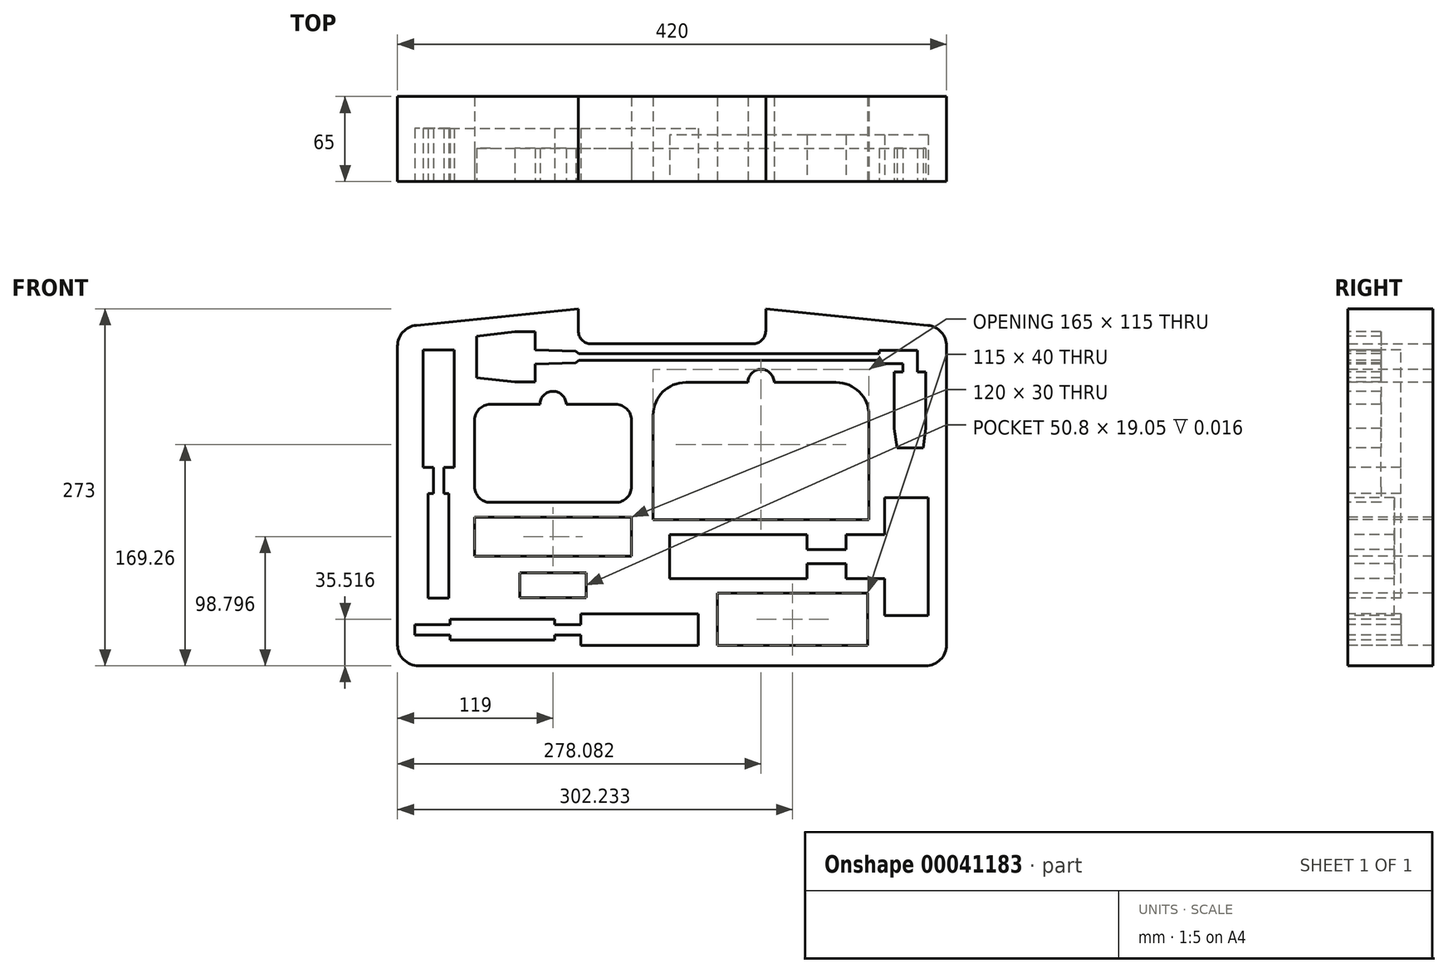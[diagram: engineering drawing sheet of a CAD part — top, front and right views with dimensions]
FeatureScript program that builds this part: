
annotation { "Feature Type Name" : "Feature", "Feature Type Description" : "" }
export const myFeature = defineFeature(function(context is Context, id is Id, definition is map)
    precondition{}
    {
        {
            var Q0;
            Q0=qCreatedBy(makeId("Front.planeOp"),FACE);
            var sketch = newSketch(context, id + "F0", { "sketchPlane" : qUnion([Q0])});
            skLineSegment(sketch, "E0.rect.top", {"start": v(0, -129.5) * mm, "end": v(-194, -129.5) * mm});
            skPoint(sketch, "E0.rect.middle", {"position": v(0, 0) * mm});
            skLineSegment(sketch, "E1", {"start": v(0, -129.5) * mm, "end": v(0, 143.5) * mm, "construction": true});
            skLineSegment(sketch, "E2", {"start": v(0, 143.5) * mm, "end": v(-71.7, 143.5) * mm, "construction": true});
            skLineSegment(sketch, "E3", {"start": v(-71.7, 143.5) * mm, "end": v(-71.7, 126.7) * mm});
            skLineSegment(sketch, "E4", {"start": v(-61.7, 116.7) * mm, "end": v(0, 116.7) * mm});
            skLineSegment(sketch, "E5", {"start": v(-71.7, 143.5) * mm, "end": v(-195.61, 130.96) * mm});
            skLineSegment(sketch, "E6", {"start": v(-210, -113.5) * mm, "end": v(-210, 115.04) * mm});
            skPoint(sketch, "E7", {"position": v(-210, 0) * mm});
            skPoint(sketch, "E8.visualSharp", {"position": v(-210, -129.5) * mm});
            skArc(sketch, "E8.filletArc", {"start": v(-210, -113.5) * mm, "mid": v(-205.31, -124.81) * mm, "end": v(-194, -129.5) * mm});
            skPoint(sketch, "E9.visualSharp", {"position": v(-210, 129.5) * mm});
            skArc(sketch, "E9.filletArc", {"start": v(-195.61, 130.96) * mm, "mid": v(-205.87, 125.77) * mm, "end": v(-210, 115.04) * mm});
            skPoint(sketch, "E10.visualSharp", {"position": v(-71.7, 116.7) * mm});
            skArc(sketch, "E10.filletArc", {"start": v(-71.7, 126.7) * mm, "mid": v(-68.77, 119.63) * mm, "end": v(-61.7, 116.7) * mm});
            skLineSegment(sketch, "E11.MirrorCS", {"start": v(71.7, 143.5) * mm, "end": v(71.7, 126.7) * mm});
            skArc(sketch, "E12.MirrorCS", {"start": v(71.7, 126.7) * mm, "mid": v(68.77, 119.63) * mm, "end": v(61.7, 116.7) * mm});
            skArc(sketch, "E13.MirrorCS", {"start": v(195.61, 130.96) * mm, "mid": v(205.87, 125.77) * mm, "end": v(210, 115.04) * mm});
            skArc(sketch, "E14.MirrorCS", {"start": v(210, -113.5) * mm, "mid": v(205.31, -124.81) * mm, "end": v(194, -129.5) * mm});
            skLineSegment(sketch, "E15.MirrorCS", {"start": v(0, -129.5) * mm, "end": v(194, -129.5) * mm});
            skPoint(sketch, "E16.MirrorP", {"position": v(210, -129.5) * mm});
            skPoint(sketch, "E17.MirrorP", {"position": v(210, 0) * mm});
            skLineSegment(sketch, "E18.MirrorCS", {"start": v(0, 143.5) * mm, "end": v(71.7, 143.5) * mm});
            skPoint(sketch, "E19.MirrorP", {"position": v(210, 129.5) * mm});
            skLineSegment(sketch, "E20.MirrorCS", {"start": v(210, -113.5) * mm, "end": v(210, 115.04) * mm});
            skLineSegment(sketch, "E21.MirrorCS", {"start": v(61.7, 116.7) * mm, "end": v(0, 116.7) * mm});
            skPoint(sketch, "E22.MirrorP", {"position": v(71.7, 116.7) * mm});
            skLineSegment(sketch, "E23.MirrorCS", {"start": v(71.7, 143.5) * mm, "end": v(195.61, 130.96) * mm});
            skSolve(sketch);
        }
        {
            var Q0;
            Q0=makeQuery(id+"F0.imprint","IMPRINT",FACE,{"disambiguationData":[TD([[makeQuery(id+"F0.imprint","IMPRINT",EDGE,{"derivedFrom":sQuery(id+"F0.wireOp",EDGE,"E0.rect.top")}),-1.0]])]});
            extrude(context, id + "F1", {"entities" : qUnion([Q0]), "depth" : 65 * mm});
        }
        {
            var Q0;
            Q0=makeQuery(id+"F1.opExtrude","CAP_FACE",FACE,{"disambiguationData":[OSD([sQuery(id+"F0.wireOp",EDGE,"E0.rect.top"),sQuery(id+"F0.wireOp",EDGE,"E3"),sQuery(id+"F0.wireOp",EDGE,"E4"),sQuery(id+"F0.wireOp",EDGE,"E5"),sQuery(id+"F0.wireOp",EDGE,"E6"),sQuery(id+"F0.wireOp",EDGE,"E8.filletArc"),sQuery(id+"F0.wireOp",EDGE,"E9.filletArc"),sQuery(id+"F0.wireOp",EDGE,"E10.filletArc"),sQuery(id+"F0.wireOp",EDGE,"E11.MirrorCS"),sQuery(id+"F0.wireOp",EDGE,"E12.MirrorCS"),sQuery(id+"F0.wireOp",EDGE,"E13.MirrorCS"),sQuery(id+"F0.wireOp",EDGE,"E14.MirrorCS"),sQuery(id+"F0.wireOp",EDGE,"E15.MirrorCS"),sQuery(id+"F0.wireOp",EDGE,"E20.MirrorCS"),sQuery(id+"F0.wireOp",EDGE,"E21.MirrorCS"),sQuery(id+"F0.wireOp",EDGE,"E23.MirrorCS")])],"isStart":false});
            var sketch = newSketch(context, id + "F2", { "sketchPlane" : qUnion([Q0])});
            skLineSegment(sketch, "E24.bottom", {"start": v(-14.42, -17.74) * mm, "end": v(55.03, -17.74) * mm});
            skLineSegment(sketch, "E24.top", {"start": v(10.58, 87.26) * mm, "end": v(58.08, 87.26) * mm});
            skLineSegment(sketch, "E24.left", {"start": v(-14.42, -17.74) * mm, "end": v(-14.42, 62.26) * mm});
            skLineSegment(sketch, "E24.right", {"start": v(150.58, -17.74) * mm, "end": v(150.58, 62.26) * mm});
            skPoint(sketch, "E25.visualSharp", {"position": v(-14.42, 87.26) * mm});
            skArc(sketch, "E25.filletArc", {"start": v(10.58, 87.26) * mm, "mid": v(-7.1, 79.94) * mm, "end": v(-14.42, 62.26) * mm});
            skPoint(sketch, "E26.visualSharp", {"position": v(150.58, 87.26) * mm});
            skArc(sketch, "E26.filletArc", {"start": v(150.58, 62.26) * mm, "mid": v(143.26, 79.94) * mm, "end": v(125.58, 87.26) * mm});
            skArc(sketch, "E27", {"start": v(78.08, 87.26) * mm, "mid": v(68.08, 97.26) * mm, "end": v(58.08, 87.26) * mm});
            skLineSegment(sketch, "E28.trimOffspring", {"start": v(78.08, 87.26) * mm, "end": v(125.58, 87.26) * mm});
            skLineSegment(sketch, "E29.trimOffspring", {"start": v(55.03, -17.74) * mm, "end": v(150.58, -17.74) * mm});
            skSolve(sketch);
        }
        {
            var Q0;
            Q0=makeQuery(id+"F1.opExtrude","CAP_FACE",FACE,{"disambiguationData":[OSD([sQuery(id+"F0.wireOp",EDGE,"E0.rect.top"),sQuery(id+"F0.wireOp",EDGE,"E3"),sQuery(id+"F0.wireOp",EDGE,"E4"),sQuery(id+"F0.wireOp",EDGE,"E5"),sQuery(id+"F0.wireOp",EDGE,"E6"),sQuery(id+"F0.wireOp",EDGE,"E8.filletArc"),sQuery(id+"F0.wireOp",EDGE,"E9.filletArc"),sQuery(id+"F0.wireOp",EDGE,"E10.filletArc"),sQuery(id+"F0.wireOp",EDGE,"E11.MirrorCS"),sQuery(id+"F0.wireOp",EDGE,"E12.MirrorCS"),sQuery(id+"F0.wireOp",EDGE,"E13.MirrorCS"),sQuery(id+"F0.wireOp",EDGE,"E14.MirrorCS"),sQuery(id+"F0.wireOp",EDGE,"E15.MirrorCS"),sQuery(id+"F0.wireOp",EDGE,"E20.MirrorCS"),sQuery(id+"F0.wireOp",EDGE,"E21.MirrorCS"),sQuery(id+"F0.wireOp",EDGE,"E23.MirrorCS")])],"isStart":false});
            var sketch = newSketch(context, id + "F3", { "sketchPlane" : qUnion([Q0])});
            skLineSegment(sketch, "E30.bottom", {"start": v(-139, -4.53) * mm, "end": v(-101.01, -4.53) * mm});
            skLineSegment(sketch, "E30.top", {"start": v(-139, 70.47) * mm, "end": v(-101, 70.47) * mm});
            skLineSegment(sketch, "E30.left", {"start": v(-151, 7.47) * mm, "end": v(-151, 58.47) * mm});
            skLineSegment(sketch, "E30.right", {"start": v(-31, 7.47) * mm, "end": v(-31, 58.47) * mm});
            skPoint(sketch, "E31.visualSharp", {"position": v(-151, 70.47) * mm});
            skArc(sketch, "E31.filletArc", {"start": v(-139, 70.47) * mm, "mid": v(-147.49, 66.96) * mm, "end": v(-151, 58.47) * mm});
            skPoint(sketch, "E32.visualSharp", {"position": v(-151, -4.53) * mm});
            skArc(sketch, "E32.filletArc", {"start": v(-151, 7.47) * mm, "mid": v(-147.49, -1.01) * mm, "end": v(-139, -4.53) * mm});
            skPoint(sketch, "E33.visualSharp", {"position": v(-31, 70.47) * mm});
            skArc(sketch, "E33.filletArc", {"start": v(-31, 58.47) * mm, "mid": v(-34.51, 66.96) * mm, "end": v(-43, 70.47) * mm});
            skPoint(sketch, "E34.visualSharp", {"position": v(-31, -4.53) * mm});
            skArc(sketch, "E34.filletArc", {"start": v(-43, -4.53) * mm, "mid": v(-34.51, -1.01) * mm, "end": v(-31, 7.47) * mm});
            skArc(sketch, "E35", {"start": v(-81, 70.47) * mm, "mid": v(-91, 80.47) * mm, "end": v(-101, 70.47) * mm});
            skLineSegment(sketch, "E36.trimOffspring", {"start": v(-81, 70.47) * mm, "end": v(-43, 70.47) * mm});
            skLineSegment(sketch, "E37.trimOffspring", {"start": v(-101.01, -4.53) * mm, "end": v(-43, -4.53) * mm});
            skSolve(sketch);
        }
        {
            var Q0;
            Q0=makeQuery(id+"F1.opExtrude","CAP_FACE",FACE,{"disambiguationData":[OSD([sQuery(id+"F0.wireOp",EDGE,"E0.rect.top"),sQuery(id+"F0.wireOp",EDGE,"E3"),sQuery(id+"F0.wireOp",EDGE,"E4"),sQuery(id+"F0.wireOp",EDGE,"E5"),sQuery(id+"F0.wireOp",EDGE,"E6"),sQuery(id+"F0.wireOp",EDGE,"E8.filletArc"),sQuery(id+"F0.wireOp",EDGE,"E9.filletArc"),sQuery(id+"F0.wireOp",EDGE,"E10.filletArc"),sQuery(id+"F0.wireOp",EDGE,"E11.MirrorCS"),sQuery(id+"F0.wireOp",EDGE,"E12.MirrorCS"),sQuery(id+"F0.wireOp",EDGE,"E13.MirrorCS"),sQuery(id+"F0.wireOp",EDGE,"E14.MirrorCS"),sQuery(id+"F0.wireOp",EDGE,"E15.MirrorCS"),sQuery(id+"F0.wireOp",EDGE,"E20.MirrorCS"),sQuery(id+"F0.wireOp",EDGE,"E21.MirrorCS"),sQuery(id+"F0.wireOp",EDGE,"E23.MirrorCS")])],"isStart":false});
            var sketch = newSketch(context, id + "F4", { "sketchPlane" : qUnion([Q0])});
            skLineSegment(sketch, "E38.bottom", {"start": v(196.1, -90.99) * mm, "end": v(196.1, -45.99) * mm});
            skLineSegment(sketch, "E38.top", {"start": v(162.6, -90.99) * mm, "end": v(162.6, -62.74) * mm});
            skLineSegment(sketch, "E38.left", {"start": v(196.1, -90.99) * mm, "end": v(162.6, -90.99) * mm});
            skLineSegment(sketch, "E39", {"start": v(162.6, -62.74) * mm, "end": v(133.1, -62.74) * mm});
            skLineSegment(sketch, "E40", {"start": v(133.1, -62.74) * mm, "end": v(133.1, -51.49) * mm});
            skLineSegment(sketch, "E41", {"start": v(133.1, -51.49) * mm, "end": v(103.1, -51.49) * mm});
            skLineSegment(sketch, "E42", {"start": v(103.1, -51.49) * mm, "end": v(103.1, -62.74) * mm});
            skPoint(sketch, "E42.endSnap0", {"position": v(147.86, -62.74) * mm});
            skLineSegment(sketch, "E43", {"start": v(103.1, -62.74) * mm, "end": v(-1.9, -62.74) * mm});
            skLineSegment(sketch, "E44", {"start": v(-1.9, -62.74) * mm, "end": v(-1.9, -45.99) * mm});
            skLineSegment(sketch, "E45", {"start": v(-1.9, -45.99) * mm, "end": v(196.1, -45.99) * mm, "construction": true});
            skLineSegment(sketch, "E46.MirrorCS", {"start": v(103.1, -40.49) * mm, "end": v(103.1, -29.24) * mm});
            skLineSegment(sketch, "E47.MirrorCS", {"start": v(133.1, -40.49) * mm, "end": v(103.1, -40.49) * mm});
            skLineSegment(sketch, "E48.MirrorCS", {"start": v(-1.9, -29.24) * mm, "end": v(-1.9, -45.99) * mm});
            skLineSegment(sketch, "E49.MirrorCS", {"start": v(133.1, -29.24) * mm, "end": v(133.1, -40.49) * mm});
            skLineSegment(sketch, "E50.MirrorCS", {"start": v(103.1, -29.24) * mm, "end": v(-1.9, -29.24) * mm});
            skLineSegment(sketch, "E51.MirrorCS", {"start": v(162.6, -29.24) * mm, "end": v(133.1, -29.24) * mm});
            skLineSegment(sketch, "E52.MirrorCS", {"start": v(196.1, -0.99) * mm, "end": v(196.1, -45.99) * mm});
            skLineSegment(sketch, "E53.MirrorCS", {"start": v(162.6, -0.99) * mm, "end": v(162.6, -29.24) * mm});
            skLineSegment(sketch, "E54.MirrorCS", {"start": v(196.1, -0.99) * mm, "end": v(162.6, -0.99) * mm});
            skPoint(sketch, "E55.MirrorP", {"position": v(147.86, -29.24) * mm});
            skSolve(sketch);
        }
        {
            var Q0;
            Q0=makeQuery(id+"F1.opExtrude","CAP_FACE",FACE,{"disambiguationData":[OSD([sQuery(id+"F0.wireOp",EDGE,"E0.rect.top"),sQuery(id+"F0.wireOp",EDGE,"E3"),sQuery(id+"F0.wireOp",EDGE,"E4"),sQuery(id+"F0.wireOp",EDGE,"E5"),sQuery(id+"F0.wireOp",EDGE,"E6"),sQuery(id+"F0.wireOp",EDGE,"E8.filletArc"),sQuery(id+"F0.wireOp",EDGE,"E9.filletArc"),sQuery(id+"F0.wireOp",EDGE,"E10.filletArc"),sQuery(id+"F0.wireOp",EDGE,"E11.MirrorCS"),sQuery(id+"F0.wireOp",EDGE,"E12.MirrorCS"),sQuery(id+"F0.wireOp",EDGE,"E13.MirrorCS"),sQuery(id+"F0.wireOp",EDGE,"E14.MirrorCS"),sQuery(id+"F0.wireOp",EDGE,"E15.MirrorCS"),sQuery(id+"F0.wireOp",EDGE,"E20.MirrorCS"),sQuery(id+"F0.wireOp",EDGE,"E21.MirrorCS"),sQuery(id+"F0.wireOp",EDGE,"E23.MirrorCS")])],"isStart":false});
            var sketch = newSketch(context, id + "F5", { "sketchPlane" : qUnion([Q0])});
            skLineSegment(sketch, "E56.top", {"start": v(-186.58, -77.81) * mm, "end": v(-186.58, 2.19) * mm});
            skLineSegment(sketch, "E56.left", {"start": v(-178.58, -77.81) * mm, "end": v(-186.58, -77.81) * mm});
            skLineSegment(sketch, "E57.top", {"start": v(-182.58, 2.19) * mm, "end": v(-182.58, 22.19) * mm});
            skLineSegment(sketch, "E58", {"start": v(-178.58, -77.81) * mm, "end": v(-178.58, 112.19) * mm, "construction": true});
            skPoint(sketch, "E59", {"position": v(-178.58, 22.19) * mm});
            skLineSegment(sketch, "E60.trimOffspring", {"start": v(-182.58, 2.19) * mm, "end": v(-186.58, 2.19) * mm});
            skLineSegment(sketch, "E61.top", {"start": v(-190.58, 22.19) * mm, "end": v(-190.58, 112.19) * mm});
            skLineSegment(sketch, "E61.right", {"start": v(-178.58, 112.19) * mm, "end": v(-190.58, 112.19) * mm});
            skLineSegment(sketch, "E62.trimOffspring", {"start": v(-182.58, 22.19) * mm, "end": v(-190.58, 22.19) * mm});
            skPoint(sketch, "E63.visualSharp", {"position": v(-186.58, -77.81) * mm});
            skPoint(sketch, "E64.visualSharp", {"position": v(-186.58, 2.19) * mm});
            skPoint(sketch, "E65.visualSharp", {"position": v(-190.58, 22.19) * mm});
            skPoint(sketch, "E66.visualSharp", {"position": v(-190.58, 112.19) * mm});
            skLineSegment(sketch, "E67.MirrorCS", {"start": v(-174.58, 2.19) * mm, "end": v(-170.58, 2.19) * mm});
            skPoint(sketch, "E68.MirrorP", {"position": v(-170.58, 2.19) * mm});
            skLineSegment(sketch, "E69.MirrorCS", {"start": v(-174.58, 2.19) * mm, "end": v(-174.58, 22.19) * mm});
            skLineSegment(sketch, "E70.MirrorCS", {"start": v(-178.58, -77.81) * mm, "end": v(-170.58, -77.81) * mm});
            skLineSegment(sketch, "E71.MirrorCS", {"start": v(-170.58, -77.81) * mm, "end": v(-170.58, 2.19) * mm});
            skPoint(sketch, "E72.MirrorP", {"position": v(-170.58, -77.81) * mm});
            skPoint(sketch, "E73.MirrorP", {"position": v(-166.58, 22.19) * mm});
            skLineSegment(sketch, "E74.MirrorCS", {"start": v(-174.58, 22.19) * mm, "end": v(-166.58, 22.19) * mm});
            skLineSegment(sketch, "E75.MirrorCS", {"start": v(-178.58, 112.19) * mm, "end": v(-166.58, 112.19) * mm});
            skLineSegment(sketch, "E76.MirrorCS", {"start": v(-166.58, 22.19) * mm, "end": v(-166.58, 112.19) * mm});
            skPoint(sketch, "E77.MirrorP", {"position": v(-166.58, 112.19) * mm});
            skSolve(sketch);
        }
        {
            var Q0;
            Q0=makeQuery(id+"F1.opExtrude","CAP_FACE",FACE,{"disambiguationData":[OSD([sQuery(id+"F0.wireOp",EDGE,"E0.rect.top"),sQuery(id+"F0.wireOp",EDGE,"E3"),sQuery(id+"F0.wireOp",EDGE,"E4"),sQuery(id+"F0.wireOp",EDGE,"E5"),sQuery(id+"F0.wireOp",EDGE,"E6"),sQuery(id+"F0.wireOp",EDGE,"E8.filletArc"),sQuery(id+"F0.wireOp",EDGE,"E9.filletArc"),sQuery(id+"F0.wireOp",EDGE,"E10.filletArc"),sQuery(id+"F0.wireOp",EDGE,"E11.MirrorCS"),sQuery(id+"F0.wireOp",EDGE,"E12.MirrorCS"),sQuery(id+"F0.wireOp",EDGE,"E13.MirrorCS"),sQuery(id+"F0.wireOp",EDGE,"E14.MirrorCS"),sQuery(id+"F0.wireOp",EDGE,"E15.MirrorCS"),sQuery(id+"F0.wireOp",EDGE,"E20.MirrorCS"),sQuery(id+"F0.wireOp",EDGE,"E21.MirrorCS"),sQuery(id+"F0.wireOp",EDGE,"E23.MirrorCS")])],"isStart":false});
            var sketch = newSketch(context, id + "F6", { "sketchPlane" : qUnion([Q0])});
            skLineSegment(sketch, "E78", {"start": v(-149.41, 122.72) * mm, "end": v(-149.41, 106.72) * mm});
            skLineSegment(sketch, "E79", {"start": v(-104.66, 125.95) * mm, "end": v(-104.66, 112.2) * mm});
            skLineSegment(sketch, "E80", {"start": v(-149.41, 106.72) * mm, "end": v(182.06, 106.72) * mm, "construction": true});
            skPoint(sketch, "E81", {"position": v(-101.66, 106.72) * mm});
            skLineSegment(sketch, "E82", {"start": v(-104.66, 125.95) * mm, "end": v(-120.16, 125.95) * mm});
            skLineSegment(sketch, "E83", {"start": v(-149.41, 122.72) * mm, "end": v(-120.16, 125.95) * mm});
            skLineSegment(sketch, "E84", {"start": v(-104.66, 112.2) * mm, "end": v(-73.68, 111.22) * mm});
            skPoint(sketch, "E85.orphan", {"position": v(-149.41, 90.72) * mm});
            skLineSegment(sketch, "E86", {"start": v(-73.68, 111.22) * mm, "end": v(-71.44, 109.22) * mm});
            skLineSegment(sketch, "E87", {"start": v(-71.44, 109.22) * mm, "end": v(158.56, 109.22) * mm});
            skLineSegment(sketch, "E88", {"start": v(158.56, 109.22) * mm, "end": v(158.56, 111.72) * mm});
            skLineSegment(sketch, "E89", {"start": v(158.56, 111.72) * mm, "end": v(187.56, 111.72) * mm});
            skLineSegment(sketch, "E90", {"start": v(187.56, 111.72) * mm, "end": v(187.56, 95.22) * mm});
            skLineSegment(sketch, "E91.MirrorCS", {"start": v(-149.41, 90.72) * mm, "end": v(-149.41, 106.72) * mm});
            skLineSegment(sketch, "E92.MirrorCS", {"start": v(-149.41, 90.72) * mm, "end": v(-120.16, 87.5) * mm});
            skLineSegment(sketch, "E93.MirrorCS", {"start": v(-104.66, 87.5) * mm, "end": v(-120.16, 87.5) * mm});
            skLineSegment(sketch, "E94.MirrorCS", {"start": v(-104.66, 87.5) * mm, "end": v(-104.66, 101.25) * mm});
            skLineSegment(sketch, "E95.MirrorCS", {"start": v(-104.66, 101.25) * mm, "end": v(-73.68, 102.22) * mm});
            skLineSegment(sketch, "E96.MirrorCS", {"start": v(-73.68, 102.22) * mm, "end": v(-71.44, 104.22) * mm});
            skLineSegment(sketch, "E97.MirrorCS", {"start": v(-71.44, 104.22) * mm, "end": v(158.56, 104.22) * mm});
            skLineSegment(sketch, "E98.MirrorCS", {"start": v(158.56, 104.22) * mm, "end": v(158.56, 101.72) * mm});
            skLineSegment(sketch, "E99.MirrorCS", {"start": v(158.56, 101.72) * mm, "end": v(176.56, 101.72) * mm});
            skLineSegment(sketch, "E100", {"start": v(176.56, 101.72) * mm, "end": v(176.56, 95.22) * mm});
            skLineSegment(sketch, "E101", {"start": v(187.56, 95.22) * mm, "end": v(176.56, 95.22) * mm, "construction": true});
            skPoint(sketch, "E102.orphan", {"position": v(187.56, 101.72) * mm});
            skLineSegment(sketch, "E103", {"start": v(182.06, 95.22) * mm, "end": v(182.06, 111.72) * mm, "construction": true});
            skLineSegment(sketch, "E104", {"start": v(187.56, 95.22) * mm, "end": v(194.06, 95.22) * mm});
            skLineSegment(sketch, "E105", {"start": v(194.06, 95.22) * mm, "end": v(194.06, 52.22) * mm});
            skLineSegment(sketch, "E106", {"start": v(194.06, 52.22) * mm, "end": v(192.06, 37.22) * mm});
            skLineSegment(sketch, "E107", {"start": v(192.06, 37.22) * mm, "end": v(182.06, 37.22) * mm});
            skLineSegment(sketch, "E108", {"start": v(182.06, 95.22) * mm, "end": v(182.06, 37.22) * mm, "construction": true});
            skLineSegment(sketch, "E109.MirrorCS", {"start": v(176.56, 95.22) * mm, "end": v(170.06, 95.22) * mm});
            skLineSegment(sketch, "E110.MirrorCS", {"start": v(170.06, 95.22) * mm, "end": v(170.06, 52.22) * mm});
            skLineSegment(sketch, "E111.MirrorCS", {"start": v(170.06, 52.22) * mm, "end": v(172.06, 37.22) * mm});
            skLineSegment(sketch, "E112.MirrorCS", {"start": v(172.06, 37.22) * mm, "end": v(182.06, 37.22) * mm});
            skSolve(sketch);
        }
        {
            var Q0;
            Q0=makeQuery(id+"F6.imprint","IMPRINT",FACE,{"disambiguationData":[TD([[makeQuery(id+"F6.imprint","IMPRINT",EDGE,{"derivedFrom":sQuery(id+"F6.wireOp",EDGE,"E78")}),-1.0]])]});
            var sketch = newSketch(context, id + "F7", { "sketchPlane" : qUnion([Q0])});
            skLineSegment(sketch, "E113.top", {"start": v(-169.86, -93.98) * mm, "end": v(-89.86, -93.98) * mm});
            skLineSegment(sketch, "E113.left", {"start": v(-169.86, -97.98) * mm, "end": v(-169.86, -93.98) * mm});
            skLineSegment(sketch, "E114.top", {"start": v(-89.86, -97.98) * mm, "end": v(-69.86, -97.98) * mm});
            skLineSegment(sketch, "E115", {"start": v(-169.86, -101.98) * mm, "end": v(20.14, -101.98) * mm, "construction": true});
            skPoint(sketch, "E116", {"position": v(-69.86, -101.98) * mm});
            skLineSegment(sketch, "E117.trimOffspring", {"start": v(-89.86, -97.98) * mm, "end": v(-89.86, -93.98) * mm});
            skLineSegment(sketch, "E118.top", {"start": v(-69.86, -89.98) * mm, "end": v(20.14, -89.98) * mm});
            skLineSegment(sketch, "E118.right", {"start": v(20.14, -101.98) * mm, "end": v(20.14, -89.98) * mm});
            skLineSegment(sketch, "E119.trimOffspring", {"start": v(-69.86, -97.98) * mm, "end": v(-69.86, -89.98) * mm});
            skPoint(sketch, "E120.visualSharp", {"position": v(-169.86, -93.98) * mm});
            skPoint(sketch, "E121.visualSharp", {"position": v(-89.86, -93.98) * mm});
            skPoint(sketch, "E122.visualSharp", {"position": v(-69.86, -89.98) * mm});
            skPoint(sketch, "E123.visualSharp", {"position": v(20.14, -89.98) * mm});
            skLineSegment(sketch, "E124.MirrorCS", {"start": v(-89.86, -105.98) * mm, "end": v(-89.86, -109.98) * mm});
            skPoint(sketch, "E125.MirrorP", {"position": v(-89.86, -109.98) * mm});
            skLineSegment(sketch, "E126.MirrorCS", {"start": v(-89.86, -105.98) * mm, "end": v(-69.86, -105.98) * mm});
            skLineSegment(sketch, "E127.MirrorCS", {"start": v(-169.86, -105.98) * mm, "end": v(-169.86, -109.98) * mm});
            skLineSegment(sketch, "E128.MirrorCS", {"start": v(-169.86, -109.98) * mm, "end": v(-89.86, -109.98) * mm});
            skPoint(sketch, "E129.MirrorP", {"position": v(-169.86, -109.98) * mm});
            skPoint(sketch, "E130.MirrorP", {"position": v(-69.86, -113.98) * mm});
            skLineSegment(sketch, "E131.MirrorCS", {"start": v(-69.86, -105.98) * mm, "end": v(-69.86, -113.98) * mm});
            skLineSegment(sketch, "E132.MirrorCS", {"start": v(20.14, -101.98) * mm, "end": v(20.14, -113.98) * mm});
            skLineSegment(sketch, "E133.MirrorCS", {"start": v(-69.86, -113.98) * mm, "end": v(20.14, -113.98) * mm});
            skPoint(sketch, "E134.MirrorP", {"position": v(20.14, -113.98) * mm});
            skLineSegment(sketch, "E135", {"start": v(-169.86, -97.98) * mm, "end": v(-196.86, -97.98) * mm});
            skPoint(sketch, "E135.endSnap0", {"position": v(-169.86, -97.98) * mm});
            skLineSegment(sketch, "E136", {"start": v(-169.86, -101.98) * mm, "end": v(-240, -101.98) * mm, "construction": true});
            skLineSegment(sketch, "E137", {"start": v(-196.86, -97.98) * mm, "end": v(-196.86, -101.98) * mm});
            skLineSegment(sketch, "E138.MirrorCS", {"start": v(-196.86, -105.98) * mm, "end": v(-196.86, -101.98) * mm});
            skLineSegment(sketch, "E139.MirrorCS", {"start": v(-169.86, -105.98) * mm, "end": v(-196.86, -105.98) * mm});
            skPoint(sketch, "E140.orphan", {"position": v(-169.86, -101.98) * mm});
            skSolve(sketch);
        }
        {
            var Q0;
            Q0=makeQuery(id+"F6.imprint","IMPRINT",FACE,{"disambiguationData":[TD([[makeQuery(id+"F6.imprint","IMPRINT",EDGE,{"derivedFrom":sQuery(id+"F6.wireOp",EDGE,"E78")}),-1.0]])]});
            var sketch = newSketch(context, id + "F8", { "sketchPlane" : qUnion([Q0])});
            skLineSegment(sketch, "E141.bottom", {"start": v(34.73, -73.98) * mm, "end": v(149.73, -73.98) * mm});
            skLineSegment(sketch, "E141.top", {"start": v(34.73, -113.98) * mm, "end": v(149.73, -113.98) * mm});
            skLineSegment(sketch, "E141.left", {"start": v(34.73, -73.98) * mm, "end": v(34.73, -113.98) * mm});
            skLineSegment(sketch, "E141.right", {"start": v(149.73, -73.98) * mm, "end": v(149.73, -113.98) * mm});
            skSolve(sketch);
        }
        {
            var Q0;
            Q0=makeQuery(id+"F6.imprint","IMPRINT",FACE,{"disambiguationData":[TD([[makeQuery(id+"F6.imprint","IMPRINT",EDGE,{"derivedFrom":sQuery(id+"F6.wireOp",EDGE,"E78")}),-1.0]])]});
            var sketch = newSketch(context, id + "F9", { "sketchPlane" : qUnion([Q0])});
            skLineSegment(sketch, "E142.bottom", {"start": v(-151, -45.7) * mm, "end": v(-151, -15.7) * mm});
            skLineSegment(sketch, "E142.top", {"start": v(-31, -45.7) * mm, "end": v(-31, -15.7) * mm});
            skLineSegment(sketch, "E142.left", {"start": v(-151, -45.7) * mm, "end": v(-31, -45.7) * mm});
            skLineSegment(sketch, "E142.right", {"start": v(-151, -15.7) * mm, "end": v(-31, -15.7) * mm});
            skSolve(sketch);
        }
        {
            var Q0;
            Q0=makeQuery(id+"F2.imprint","IMPRINT",FACE,{"disambiguationData":[TD([[makeQuery(id+"F2.imprint","IMPRINT",EDGE,{"derivedFrom":sQuery(id+"F2.wireOp",EDGE,"E24.bottom")}),-1.0]])]});
            var sketch = newSketch(context, id + "F10", { "sketchPlane" : qUnion([Q0])});
            skLineSegment(sketch, "E143.bottom", {"start": v(-116.4, -58.4) * mm, "end": v(-65.6, -58.4) * mm});
            skLineSegment(sketch, "E143.top", {"start": v(-116.4, -77.46) * mm, "end": v(-65.6, -77.46) * mm});
            skLineSegment(sketch, "E143.left", {"start": v(-116.4, -58.4) * mm, "end": v(-116.4, -77.46) * mm});
            skLineSegment(sketch, "E143.right", {"start": v(-65.6, -58.4) * mm, "end": v(-65.6, -77.46) * mm});
            skLineSegment(sketch, "E144.0", {"start": v(-151, -45.7) * mm, "end": v(-31, -45.7) * mm, "construction": true});
            skLineSegment(sketch, "E145", {"start": v(-91, -45.7) * mm, "end": v(-91, -87.53) * mm, "construction": true});
            skPoint(sketch, "E146", {"position": v(-91, -58.4) * mm});
            skSolve(sketch);
        }
        {
            var Q0;
            Q0=makeQuery(id+"F10.imprint","IMPRINT",FACE,{"disambiguationData":[TD([[makeQuery(id+"F10.imprint","IMPRINT",EDGE,{"derivedFrom":makeQuery(id+"F2.imprint","IMPRINT",EDGE,{"derivedFrom":sQuery(id+"F2.wireOp",EDGE,"E24.bottom")})}),1.0]])]});
            extrude(context, id + "F11", {"entities" : qUnion([Q0]), "operationType" : NewBodyOperationType.REMOVE, "endBound" : BoundingType.THROUGH_ALL, "oppositeDirection" : true, "depth" : 25 * mm});
        }
        {
            var Q0;
            Q0 = qSketchRegion(id + "F3", true);
            extrude(context, id + "F12", {"entities" : qUnion([Q0]), "operationType" : NewBodyOperationType.REMOVE, "oppositeDirection" : true, "depth" : 25.4 * mm});
        }
        {
            var Q0;
            Q0 = qSketchRegion(id + "F4", true);
            extrude(context, id + "F13", {"entities" : qUnion([Q0]), "operationType" : NewBodyOperationType.REMOVE, "oppositeDirection" : true, "depth" : 35.56 * mm});
        }
        {
            var Q0;
            Q0 = qSketchRegion(id + "F9", true);
            var Q1;
            Q1 = qSketchRegion(id + "F8", true);
            extrude(context, id + "F14", {"entities" : qUnion([Q0, Q1]), "operationType" : NewBodyOperationType.REMOVE, "endBound" : BoundingType.THROUGH_ALL, "oppositeDirection" : true, "depth" : 25 * mm});
        }
        {
            var Q0;
            Q0=makeQuery(id+"F7.imprint","IMPRINT",FACE,{"disambiguationData":[TD([[makeQuery(id+"F7.imprint","IMPRINT",EDGE,{"derivedFrom":makeQuery(id+"F6.imprint","IMPRINT",EDGE,{"derivedFrom":sQuery(id+"F6.wireOp",EDGE,"E78")})}),1.0]])]});
            extrude(context, id + "F15", {"entities" : qUnion([Q0]), "operationType" : NewBodyOperationType.REMOVE, "oppositeDirection" : true, "depth" : 25.4 * mm});
        }
        {
            var Q0;
            Q0=makeQuery(id+"F7.imprint","IMPRINT",FACE,{"disambiguationData":[TD([[makeQuery(id+"F7.imprint","IMPRINT",EDGE,{"derivedFrom":sQuery(id+"F7.wireOp",EDGE,"E113.top")}),-1.0]])]});
            var Q1;
            Q1=makeQuery(id+"F5.imprint","IMPRINT",FACE,{"disambiguationData":[TD([[makeQuery(id+"F5.imprint","IMPRINT",EDGE,{"derivedFrom":sQuery(id+"F5.wireOp",EDGE,"E56.top")}),-1.0]])]});
            extrude(context, id + "F16", {"entities" : qUnion([Q0, Q1]), "operationType" : NewBodyOperationType.REMOVE, "oppositeDirection" : true, "depth" : 40.64 * mm});
        }
        {
            var Q0;
            Q0 = qSketchRegion(id + "F10", true);
            extrude(context, id + "F17", {"entities" : qUnion([Q0]), "operationType" : NewBodyOperationType.REMOVE, "oppositeDirection" : true, "depth" : 2 / 127 * mm});
        }
    });
